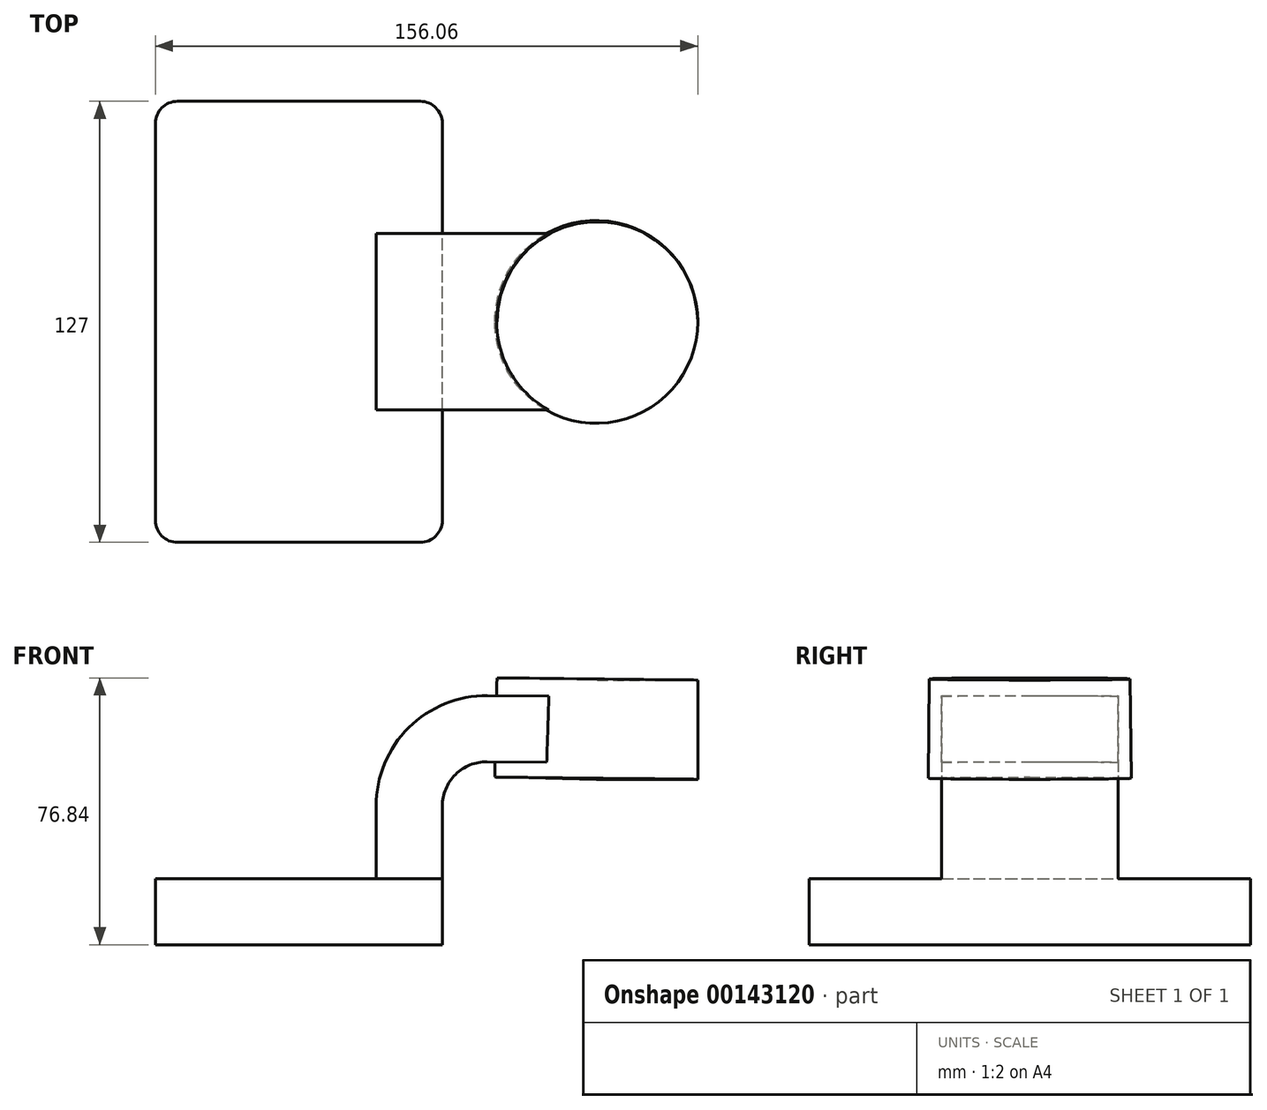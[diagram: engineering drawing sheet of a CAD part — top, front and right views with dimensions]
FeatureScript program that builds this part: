
annotation { "Feature Type Name" : "Feature", "Feature Type Description" : "" }
export const myFeature = defineFeature(function(context is Context, id is Id, definition is map)
    precondition{}
    {
        {
            var Q0;
            Q0=qCreatedBy(makeId("Front.planeOp"),FACE);
            var sketch = newSketch(context, id + "F0", { "sketchPlane" : qUnion([Q0])});
            skLineSegment(sketch, "E0.bottom", {"start": v(41.27, 9.53) * mm, "end": v(-41.28, 9.53) * mm});
            skLineSegment(sketch, "E0.top", {"start": v(41.28, -9.52) * mm, "end": v(-41.27, -9.53) * mm});
            skLineSegment(sketch, "E0.left", {"start": v(41.28, 9.53) * mm, "end": v(41.28, -9.52) * mm});
            skLineSegment(sketch, "E0.right", {"start": v(-41.28, 9.53) * mm, "end": v(-41.28, -9.52) * mm});
            skPoint(sketch, "E0.middle", {"position": v(0, 0) * mm});
            skLineSegment(sketch, "E1.bottom", {"start": v(63.99, 66.67) * mm, "end": v(114.79, 66.67) * mm});
            skLineSegment(sketch, "E1.top", {"start": v(63.99, 38.1) * mm, "end": v(114.79, 38.1) * mm});
            skLineSegment(sketch, "E1.left", {"start": v(63.99, 66.67) * mm, "end": v(63.99, 38.1) * mm});
            skLineSegment(sketch, "E1.right", {"start": v(114.79, 66.67) * mm, "end": v(114.79, 38.1) * mm});
            skLineSegment(sketch, "E2", {"start": v(41.27, 9.53) * mm, "end": v(41.27, 30.4) * mm});
            skArc(sketch, "E3", {"start": v(41.27, 30.4) * mm, "mid": v(45.05, 39.46) * mm, "end": v(54.15, 43.16) * mm});
            skLineSegment(sketch, "E4", {"start": v(85.72, 42.88) * mm, "end": v(54.15, 43.16) * mm});
            skPoint(sketch, "E5", {"position": v(89.39, 38.1) * mm});
            skLineSegment(sketch, "E6.0", {"start": v(85.9, 61.92) * mm, "end": v(54.32, 62.2) * mm});
            skArc(sketch, "E6.1", {"start": v(22.22, 30.4) * mm, "mid": v(31.64, 52.99) * mm, "end": v(54.32, 62.2) * mm});
            skLineSegment(sketch, "E6.2", {"start": v(22.22, 9.53) * mm, "end": v(22.22, 30.4) * mm});
            skFitSpline(sketch, "E7", {"points": [v(-41.28, 9.53) * mm, v(54.32, 62.2) * mm], "startDerivative": vector(25.07, 74) * mm, "endDerivative": vector(86.17, -39.57) * mm});
            skLineSegment(sketch, "E8", {"start": v(85.58, 38.1) * mm, "end": v(85.9, 66.67) * mm});
            skSolve(sketch);
        }
        {
            var Q0;
            Q0=makeQuery(id+"F0.imprint","IMPRINT",FACE,{"disambiguationData":[TD([[makeQuery(id+"F0.imprint","IMPRINT",EDGE,{"derivedFrom":sQuery(id+"F0.wireOp",EDGE,"E0.top")}),-1.0]])]});
            extrude(context, id + "F1", {"entities" : qUnion([Q0]), "endBound" : BoundingType.SYMMETRIC, "depth" : 127 * mm});
        }
        {
            var Q0;
            {var subQ0=sQuery(id+"F0.wireOp",EDGE,"E6.0");var subQ1=sQuery(id+"F0.wireOp",EDGE,"E1.left");var subQ2=makeQuery(id+"F0.imprint","INTERSECT",VERTEX,{"derivedFrom":[subQ1,subQ0]});Q0=makeQuery(id+"F0.imprint","IMPRINT",FACE,{"disambiguationData":[TD([[makeQuery(id+"F0.imprint","IMPRINT",EDGE,{"disambiguationData":[TD([[subQ2,-1.0]])],"derivedFrom":subQ1}),1.0]])]});}
            var Q1;
            {var subQ5=sQuery(id+"F0.wireOp",EDGE,"E2");Q1=makeQuery(id+"F0.imprint","IMPRINT",FACE,{"disambiguationData":[TD([[makeQuery(id+"F0.imprint","IMPRINT",EDGE,{"derivedFrom":subQ5}),1.0]])]});}
            extrude(context, id + "F2", {"entities" : qUnion([Q0, Q1]), "operationType" : NewBodyOperationType.ADD, "endBound" : BoundingType.SYMMETRIC, "depth" : 50.8 * mm});
        }
        {
            var Q0;
            Q0=makeQuery(id+"F0.imprint","IMPRINT",FACE,{"disambiguationData":[TD([[makeQuery(id+"F0.imprint","IMPRINT",EDGE,{"derivedFrom":sQuery(id+"F0.wireOp",EDGE,"E6.1")}),1.0]])]});
            extrude(context, id + "F3", {"entities" : qUnion([Q0]), "operationType" : NewBodyOperationType.ADD, "endBound" : BoundingType.SYMMETRIC, "depth" : 15.88 * mm});
        }
        {
            var Q0;
            {var subQ0=sQuery(id+"F0.wireOp",EDGE,"E1.right");Q0=makeQuery(id+"F0.imprint","IMPRINT",FACE,{"disambiguationData":[TD([[makeQuery(id+"F0.imprint","IMPRINT",EDGE,{"derivedFrom":subQ0}),-1.0]])]});}
            var Q1;
            Q1=sQuery(id+"F0.wireOp",EDGE,"E8");
            revolve(context, id + "F4", {"operationType" : NewBodyOperationType.ADD, "entities" : qUnion([Q0]), "axis" : qUnion([Q1]), "revolveType" : RevolveType.FULL});
        }
        {
            var Q0;
            Q0=makeQuery(id+"F1.opExtrude","CAP_EDGE",EDGE,{"disambiguationData":[OSD([sQuery(id+"F0.wireOp",EDGE,"E0.right")])],"isStart":false});
            var Q1;
            Q1=makeQuery(id+"F1.opExtrude","CAP_EDGE",EDGE,{"disambiguationData":[OSD([sQuery(id+"F0.wireOp",EDGE,"E0.left")])],"isStart":false});
            var Q2;
            Q2=makeQuery(id+"F1.opExtrude","CAP_EDGE",EDGE,{"disambiguationData":[OSD([sQuery(id+"F0.wireOp",EDGE,"E0.left")])],"isStart":true});
            var Q3;
            Q3=makeQuery(id+"F1.opExtrude","CAP_EDGE",EDGE,{"disambiguationData":[OSD([sQuery(id+"F0.wireOp",EDGE,"E0.right")])],"isStart":true});
            fillet(context, id + "F5", {"entities" : qUnion([Q0, Q1, Q2, Q3]), "radius" : 6.35 * mm, "tangentPropagation" : true, "allowEdgeOverflow" : false});
        }
    });
